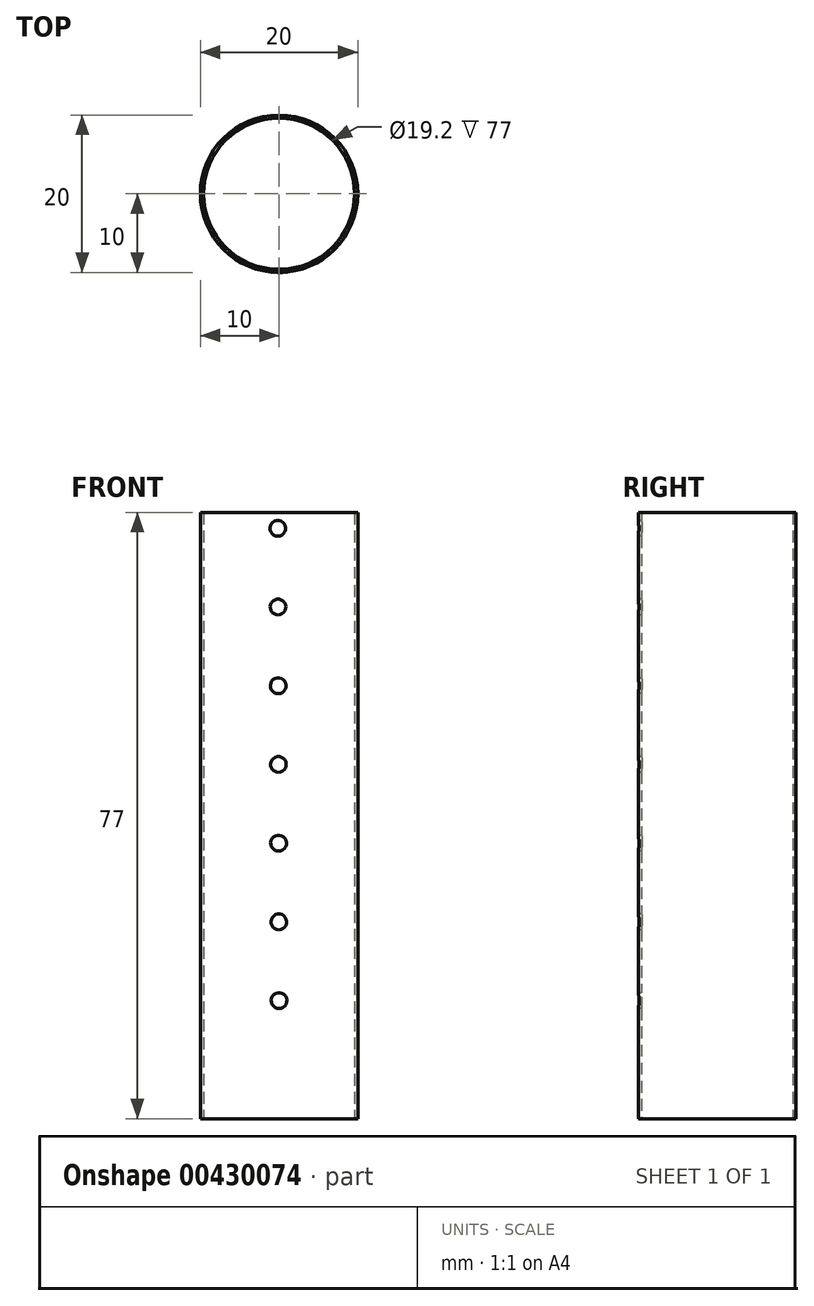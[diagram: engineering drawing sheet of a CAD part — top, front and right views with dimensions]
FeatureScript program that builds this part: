
annotation { "Feature Type Name" : "Feature", "Feature Type Description" : "" }
export const myFeature = defineFeature(function(context is Context, id is Id, definition is map)
    precondition{}
    {
        {
            var Q0;
            Q0=qCreatedBy(makeId("Top.planeOp"),FACE);
            var sketch = newSketch(context, id + "F0", { "sketchPlane" : qUnion([Q0])});
            skCircle(sketch, "E0", {"center": v(0, 0) * mm, "radius": 10 * mm});
            skCircle(sketch, "E1", {"center": v(0, 0) * mm, "radius": 9.6 * mm});
            skSolve(sketch);
        }
        {
            var Q0;
            Q0=makeQuery(id+"F0.imprint","IMPRINT",FACE,{"disambiguationData":[TD([[makeQuery(id+"F0.imprint","IMPRINT",EDGE,{"derivedFrom":sQuery(id+"F0.wireOp",EDGE,"E0")}),1.0]])]});
            extrude(context, id + "F1", {"entities" : qUnion([Q0]), "depth" : (7 * 10 + 7) * mm});
        }
        {
            var Q0;
            Q0=qCreatedBy(makeId("Front.planeOp"),FACE);
            cPlane(context, id + "F2", {"entities" : qUnion([Q0]), "cplaneType" : CPlaneType.OFFSET, "offset" : 10 * mm, "width" : 150 * mm, "height" : 150 * mm});
        }
        {
            var Q0;
            Q0=qCreatedBy(id+"F2.planeOp",FACE);
            var sketch = newSketch(context, id + "F3", { "sketchPlane" : qUnion([Q0])});
            skCircle(sketch, "E2", {"center": v(0, 15) * mm, "radius": 1 * mm});
            skCircle(sketch, "E3.1.0.0", {"center": v(-0.03, 25) * mm, "radius": 1 * mm});
            skCircle(sketch, "E3.2.0.0", {"center": v(-0.05, 35) * mm, "radius": 1 * mm});
            skCircle(sketch, "E3.3.0.0", {"center": v(-0.08, 45) * mm, "radius": 1 * mm});
            skCircle(sketch, "E3.4.0.0", {"center": v(-0.1, 55) * mm, "radius": 1 * mm});
            skCircle(sketch, "E3.5.0.0", {"center": v(-0.13, 65) * mm, "radius": 1 * mm});
            skCircle(sketch, "E3.6.0.0", {"center": v(-0.16, 75) * mm, "radius": 1 * mm});
            skLineSegment(sketch, "E3.direction1", {"start": v(0, 15) * mm, "end": v(-0.03, 25) * mm, "construction": true});
            skSolve(sketch);
        }
        {
            var Q0;
            Q0=qSketchRegion(id+"F3",true);
            extrude(context, id + "F4", {"entities" : qUnion([Q0]), "operationType" : NewBodyOperationType.REMOVE, "oppositeDirection" : true, "depth" : 10 * mm});
        }
    });
